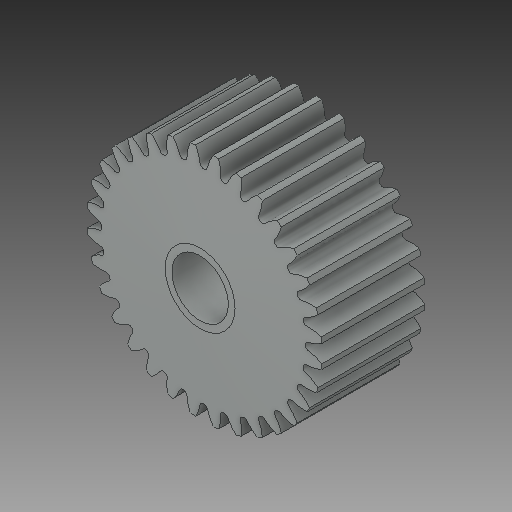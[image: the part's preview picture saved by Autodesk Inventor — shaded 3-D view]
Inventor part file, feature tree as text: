
AUTODESK INVENTOR PART (.ipt)
format: ipt  version: 2018 (Build 220112000, 112)  size: 511,488 bytes
history: native  units: in
note: dims shown in document units (in); Inventor stores cm internally (conversion verified against a paired STEP export)
features: mirror x1
ambient origin geometry x8: Origin, YZ Plane, XZ Plane, XY Plane, X Axis, Y Axis, Z Axis, Center Point
bodies: Solid1 (feature_tree)
feature tree (1):
  mirror  "Mirror1"
